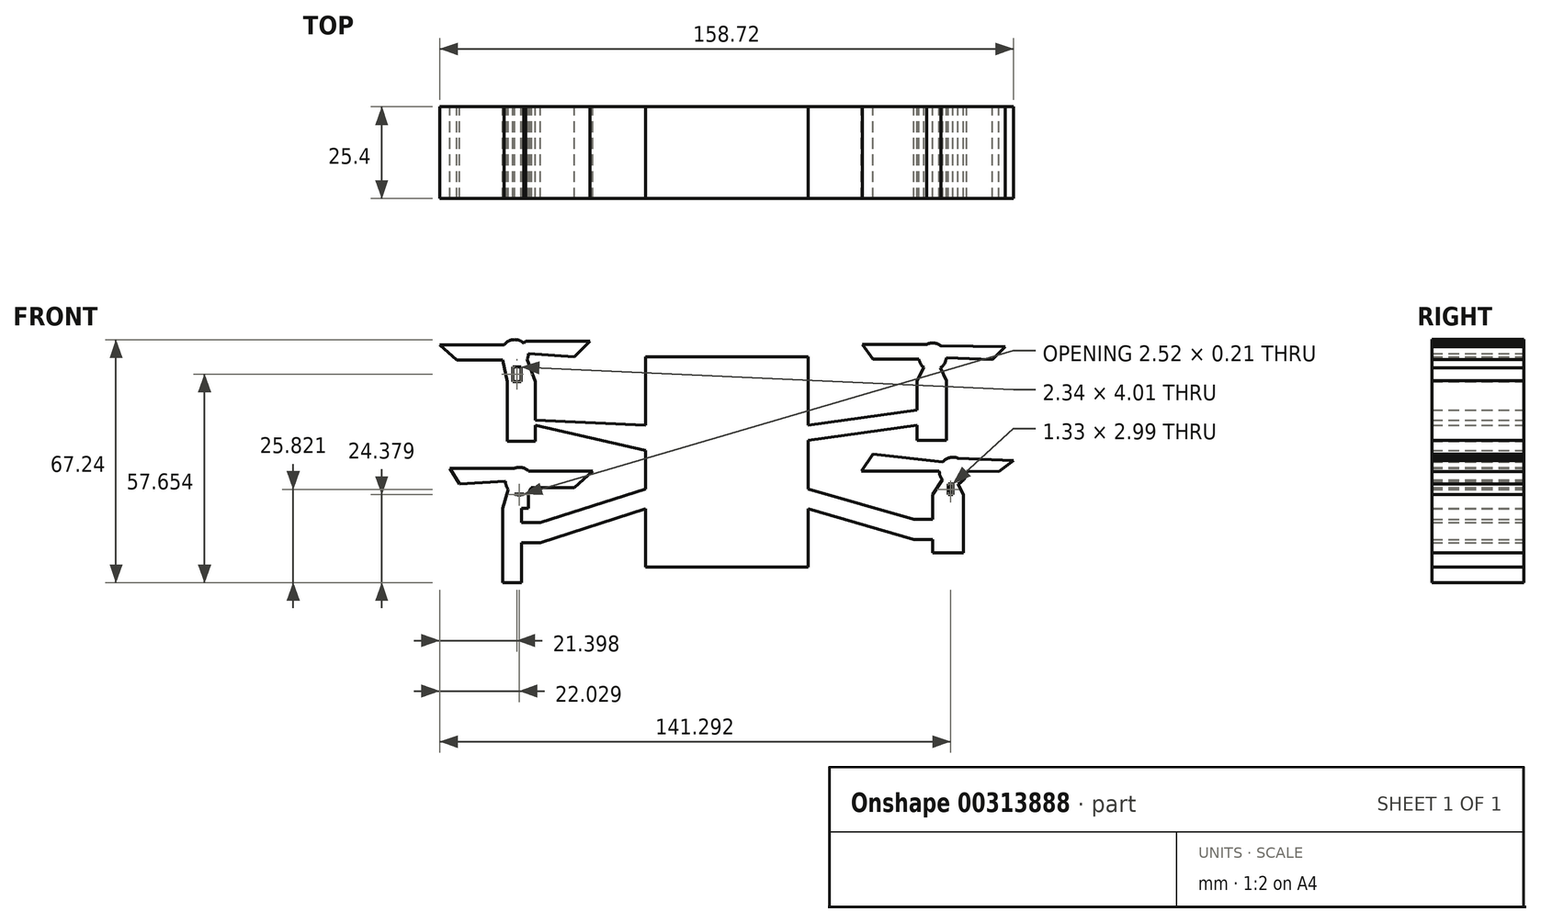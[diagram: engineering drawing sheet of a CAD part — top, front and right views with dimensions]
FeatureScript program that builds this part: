
annotation { "Feature Type Name" : "Feature", "Feature Type Description" : "" }
export const myFeature = defineFeature(function(context is Context, id is Id, definition is map)
    precondition{}
    {
        {
            var Q0;
            Q0=qCreatedBy(makeId("Front.planeOp"),FACE);
            var sketch = newSketch(context, id + "F0", { "sketchPlane" : qUnion([Q0])});
            skLineSegment(sketch, "E0.bottom", {"start": v(-22.4, 18.93) * mm, "end": v(22.55, 18.93) * mm});
            skLineSegment(sketch, "E0.top", {"start": v(-22.4, -39.27) * mm, "end": v(22.55, -39.27) * mm});
            skLineSegment(sketch, "E0.left", {"start": v(-22.4, 18.93) * mm, "end": v(-22.4, -39.27) * mm});
            skLineSegment(sketch, "E0.right", {"start": v(22.55, 18.93) * mm, "end": v(22.55, -39.27) * mm});
            skLineSegment(sketch, "E1", {"start": v(-22.4, 0) * mm, "end": v(-52.86, 1.38) * mm});
            skLineSegment(sketch, "E2", {"start": v(-52.86, 1.38) * mm, "end": v(-52.86, 12.1) * mm});
            skLineSegment(sketch, "E3", {"start": v(-52.86, 12.1) * mm, "end": v(-60.65, 12.1) * mm});
            skLineSegment(sketch, "E4", {"start": v(-60.65, 12.1) * mm, "end": v(-60.65, 1.38) * mm});
            skLineSegment(sketch, "E5", {"start": v(-60.65, 1.38) * mm, "end": v(-60.65, -4.45) * mm});
            skLineSegment(sketch, "E6", {"start": v(-60.65, -4.45) * mm, "end": v(-52.86, -4.45) * mm});
            skLineSegment(sketch, "E7", {"start": v(-52.86, -4.45) * mm, "end": v(-52.86, 0) * mm});
            skLineSegment(sketch, "E8", {"start": v(-52.86, 0) * mm, "end": v(-22.4, -6.97) * mm});
            skLineSegment(sketch, "E9", {"start": v(22.55, 0) * mm, "end": v(52.74, 4.2) * mm});
            skLineSegment(sketch, "E10", {"start": v(52.74, 4.2) * mm, "end": v(52.74, 12.27) * mm});
            skLineSegment(sketch, "E11", {"start": v(52.74, 12.27) * mm, "end": v(60.79, 12.27) * mm});
            skLineSegment(sketch, "E12", {"start": v(60.79, 12.27) * mm, "end": v(60.79, -4.2) * mm});
            skLineSegment(sketch, "E13", {"start": v(60.79, -4.2) * mm, "end": v(52.74, -4.2) * mm});
            skLineSegment(sketch, "E14", {"start": v(52.74, -4.2) * mm, "end": v(52.74, 0) * mm});
            skLineSegment(sketch, "E15", {"start": v(52.74, 0) * mm, "end": v(22.55, -4.2) * mm});
            skLineSegment(sketch, "E16", {"start": v(22.55, -4.2) * mm, "end": v(22.55, -17.6) * mm});
            skLineSegment(sketch, "E17", {"start": v(22.55, -17.6) * mm, "end": v(51.82, -26.07) * mm});
            skLineSegment(sketch, "E18", {"start": v(51.82, -26.07) * mm, "end": v(57.04, -26.07) * mm});
            skLineSegment(sketch, "E19", {"start": v(57.04, -26.07) * mm, "end": v(57.04, -19.22) * mm});
            skLineSegment(sketch, "E20", {"start": v(57.04, -19.22) * mm, "end": v(65.57, -19.22) * mm});
            skLineSegment(sketch, "E21", {"start": v(65.57, -19.22) * mm, "end": v(65.57, -35.25) * mm});
            skLineSegment(sketch, "E22", {"start": v(65.57, -35.25) * mm, "end": v(57.04, -35.25) * mm});
            skLineSegment(sketch, "E23", {"start": v(57.04, -35.25) * mm, "end": v(57.04, -31.65) * mm});
            skLineSegment(sketch, "E24", {"start": v(57.04, -31.65) * mm, "end": v(51.82, -31.65) * mm});
            skLineSegment(sketch, "E25", {"start": v(51.82, -31.65) * mm, "end": v(22.55, -23.17) * mm});
            skLineSegment(sketch, "E26", {"start": v(-22.4, -17.6) * mm, "end": v(-51.43, -26.9) * mm});
            skLineSegment(sketch, "E27", {"start": v(-51.43, -26.9) * mm, "end": v(-56.64, -26.9) * mm});
            skLineSegment(sketch, "E28", {"start": v(-56.64, -26.9) * mm, "end": v(-56.64, -22.98) * mm});
            skLineSegment(sketch, "E29", {"start": v(-56.64, -22.98) * mm, "end": v(-61.86, -22.98) * mm});
            skLineSegment(sketch, "E30", {"start": v(-61.86, -22.98) * mm, "end": v(-61.86, -43.55) * mm});
            skLineSegment(sketch, "E31", {"start": v(-61.86, -43.55) * mm, "end": v(-56.64, -43.55) * mm});
            skLineSegment(sketch, "E32", {"start": v(-56.64, -43.55) * mm, "end": v(-56.64, -32.48) * mm});
            skLineSegment(sketch, "E33", {"start": v(-56.64, -32.48) * mm, "end": v(-51.43, -32.48) * mm});
            skLineSegment(sketch, "E34", {"start": v(-51.43, -32.48) * mm, "end": v(-22.4, -23.17) * mm});
            skLineSegment(sketch, "E35.bottom", {"start": v(-58.55, -22.98) * mm, "end": v(-54.7, -22.98) * mm});
            skLineSegment(sketch, "E35.top", {"start": v(-58.55, -19.06) * mm, "end": v(-54.7, -19.06) * mm});
            skLineSegment(sketch, "E35.left", {"start": v(-58.55, -22.98) * mm, "end": v(-58.55, -19.06) * mm});
            skLineSegment(sketch, "E35.right", {"start": v(-54.7, -22.98) * mm, "end": v(-54.7, -19.06) * mm});
            skLineSegment(sketch, "E36.bottom", {"start": v(61.3, -19.22) * mm, "end": v(62.64, -19.22) * mm});
            skLineSegment(sketch, "E36.top", {"start": v(61.3, -16.23) * mm, "end": v(62.64, -16.23) * mm});
            skLineSegment(sketch, "E36.left", {"start": v(61.3, -19.22) * mm, "end": v(61.3, -16.23) * mm});
            skLineSegment(sketch, "E36.right", {"start": v(62.64, -19.22) * mm, "end": v(62.64, -16.23) * mm});
            skLineSegment(sketch, "E37.bottom", {"start": v(56.76, 12.27) * mm, "end": v(59.1, 12.27) * mm});
            skLineSegment(sketch, "E38.bottom", {"start": v(-56.75, 12.1) * mm, "end": v(-59.09, 12.1) * mm});
            skLineSegment(sketch, "E38.top", {"start": v(-56.75, 16.1) * mm, "end": v(-59.09, 16.1) * mm});
            skLineSegment(sketch, "E38.left", {"start": v(-56.75, 12.1) * mm, "end": v(-56.75, 16.1) * mm});
            skLineSegment(sketch, "E38.right", {"start": v(-59.09, 12.1) * mm, "end": v(-59.09, 16.1) * mm});
            skCircle(sketch, "E39", {"center": v(-57.3, -15.47) * mm, "radius": 3.81 * mm});
            skCircle(sketch, "E40", {"center": v(-58.55, 19.88) * mm, "radius": 3.81 * mm});
            skCircle(sketch, "E41", {"center": v(62.64, -12.66) * mm, "radius": 3.81 * mm});
            skLineSegment(sketch, "E42", {"start": v(-61.54, 22.24) * mm, "end": v(-79.32, 22.24) * mm});
            skLineSegment(sketch, "E43", {"start": v(-79.32, 22.24) * mm, "end": v(-74.62, 18.1) * mm});
            skLineSegment(sketch, "E44", {"start": v(-74.62, 18.1) * mm, "end": v(-61.92, 18.1) * mm});
            skLineSegment(sketch, "E45", {"start": v(-61.92, 18.1) * mm, "end": v(-55.54, 23.2) * mm});
            skLineSegment(sketch, "E46", {"start": v(-55.54, 23.2) * mm, "end": v(-37.76, 23.2) * mm});
            skLineSegment(sketch, "E47", {"start": v(58.83, -12.66) * mm, "end": v(37.36, -12.66) * mm});
            skLineSegment(sketch, "E48", {"start": v(37.36, -12.66) * mm, "end": v(40.55, -7.95) * mm});
            skLineSegment(sketch, "E49", {"start": v(40.55, -7.95) * mm, "end": v(59.8, -10.11) * mm});
            skLineSegment(sketch, "E50", {"start": v(-54.7, -12.68) * mm, "end": v(-36.92, -12.68) * mm});
            skPoint(sketch, "E50.endSnap0", {"position": v(-36.92, -27.83) * mm});
            skLineSegment(sketch, "E51", {"start": v(-36.92, -12.68) * mm, "end": v(-42, -17.24) * mm});
            skLineSegment(sketch, "E52", {"start": v(-42, -17.24) * mm, "end": v(-54.7, -17.24) * mm});
            skLineSegment(sketch, "E53", {"start": v(-58.69, -11.92) * mm, "end": v(-76.47, -11.92) * mm});
            skLineSegment(sketch, "E54", {"start": v(-76.47, -11.92) * mm, "end": v(-73.78, -16.23) * mm});
            skLineSegment(sketch, "E55", {"start": v(-73.78, -16.23) * mm, "end": v(-61.1, -15.47) * mm});
            skLineSegment(sketch, "E56", {"start": v(61.63, -8.99) * mm, "end": v(79.4, -9.78) * mm});
            skLineSegment(sketch, "E57", {"start": v(75.34, -12.83) * mm, "end": v(62.64, -12.66) * mm});
            skCircle(sketch, "E58", {"center": v(56.97, 18.93) * mm, "radius": 3.81 * mm});
            skPoint(sketch, "E58.centerSnap0", {"position": v(0.07, 18.93) * mm});
            skLineSegment(sketch, "E59", {"start": v(54.58, 15.96) * mm, "end": v(52.74, 12.27) * mm});
            skLineSegment(sketch, "E60", {"start": v(59.18, 15.83) * mm, "end": v(60.79, 12.27) * mm});
            skLineSegment(sketch, "E61", {"start": v(59.73, -15.12) * mm, "end": v(57.04, -19.22) * mm});
            skLineSegment(sketch, "E62", {"start": v(63.97, -16.23) * mm, "end": v(65.57, -19.22) * mm});
            skLineSegment(sketch, "E63", {"start": v(-54.21, -17.71) * mm, "end": v(-56.64, -22.98) * mm});
            skLineSegment(sketch, "E64", {"start": v(-60.32, -17.78) * mm, "end": v(-61.86, -22.98) * mm});
            skLineSegment(sketch, "E65", {"start": v(-61.86, 18) * mm, "end": v(-60.65, 12.1) * mm});
            skLineSegment(sketch, "E66", {"start": v(-37.76, 23.2) * mm, "end": v(-42.07, 18.98) * mm});
            skLineSegment(sketch, "E67", {"start": v(-42.07, 18.98) * mm, "end": v(-54.74, 19.87) * mm});
            skLineSegment(sketch, "E68", {"start": v(-54.74, 19.87) * mm, "end": v(-55.08, 18.32) * mm});
            skLineSegment(sketch, "E69", {"start": v(-55.08, 18.32) * mm, "end": v(-52.86, 12.1) * mm});
            skLineSegment(sketch, "E70", {"start": v(59.31, 21.93) * mm, "end": v(77.1, 21.67) * mm});
            skLineSegment(sketch, "E71", {"start": v(77.1, 21.67) * mm, "end": v(73.45, 18.12) * mm});
            skLineSegment(sketch, "E72", {"start": v(73.45, 18.12) * mm, "end": v(60.77, 18.7) * mm});
            skLineSegment(sketch, "E73", {"start": v(53.22, 18.25) * mm, "end": v(40.52, 18.25) * mm});
            skLineSegment(sketch, "E74", {"start": v(40.52, 18.25) * mm, "end": v(37.53, 22.36) * mm});
            skLineSegment(sketch, "E75", {"start": v(37.53, 22.36) * mm, "end": v(55.31, 22.36) * mm});
            skLineSegment(sketch, "E76", {"start": v(79.4, -9.78) * mm, "end": v(75.34, -12.83) * mm});
            skSolve(sketch);
        }
        {
            var Q0;
            Q0 = qSketchRegion(id + "F0", true);
            extrude(context, id + "F1", {"entities" : qUnion([Q0]), "depth" : 25.4 * mm});
        }
    });
